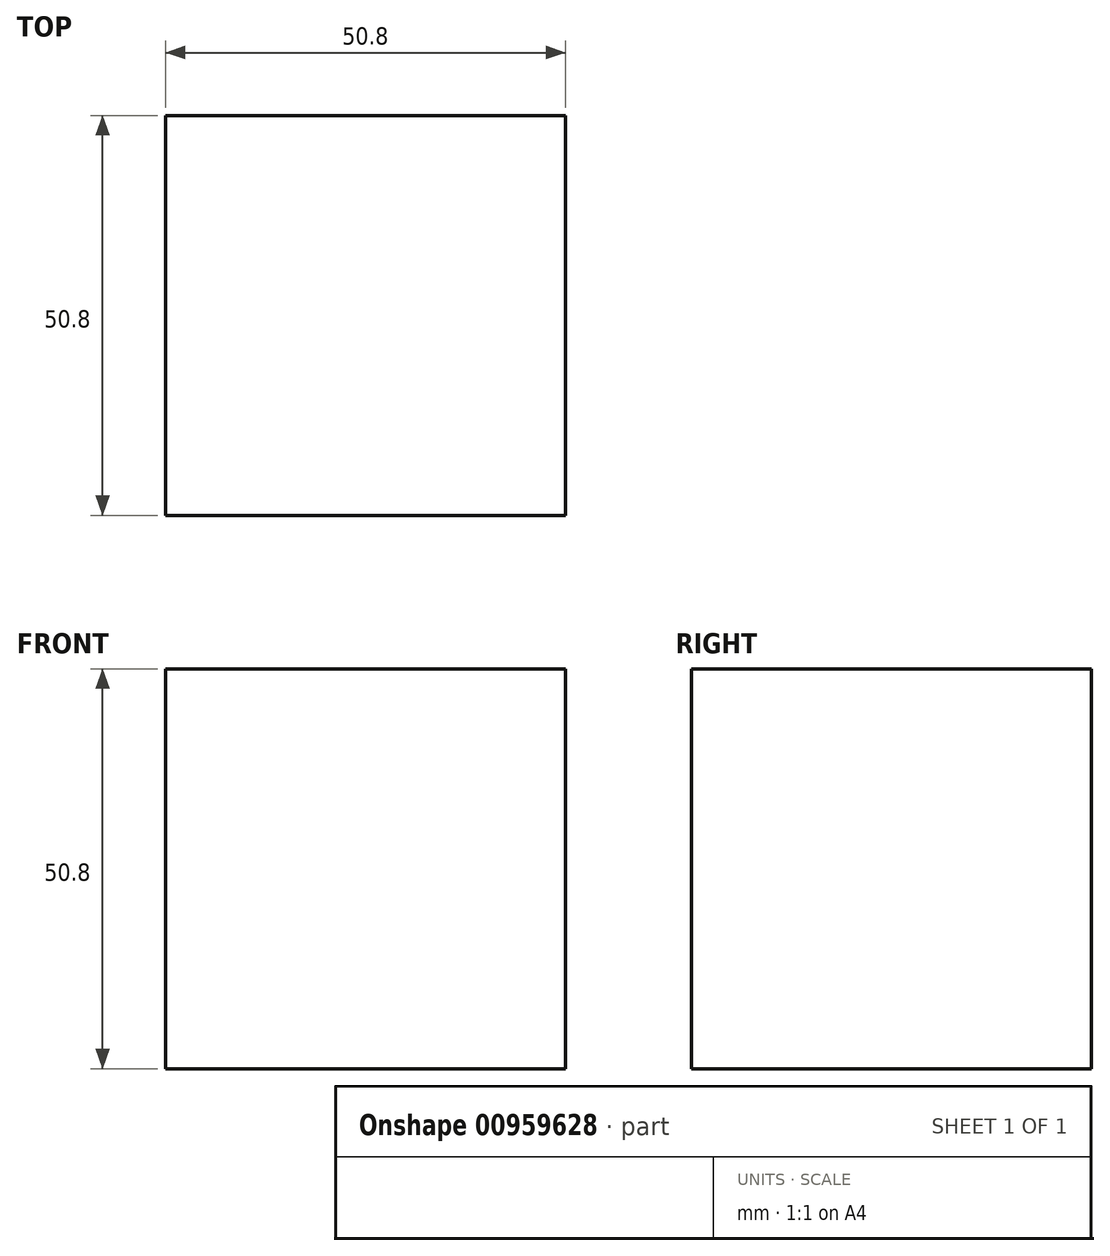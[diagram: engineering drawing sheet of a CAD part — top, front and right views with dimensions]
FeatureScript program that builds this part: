
annotation { "Feature Type Name" : "Feature", "Feature Type Description" : "" }
export const myFeature = defineFeature(function(context is Context, id is Id, definition is map)
    precondition{}
    {
        {
            var Q0;
            Q0=qCreatedBy(makeId("Top.planeOp"),FACE);
            var sketch = newSketch(context, id + "F0", { "sketchPlane" : qUnion([Q0])});
            skLineSegment(sketch, "E0.bottom", {"start": v(25.4, 25.4) * mm, "end": v(-25.4, 25.4) * mm});
            skLineSegment(sketch, "E0.top", {"start": v(25.4, -25.4) * mm, "end": v(-25.4, -25.4) * mm});
            skLineSegment(sketch, "E0.left", {"start": v(25.4, 25.4) * mm, "end": v(25.4, -25.4) * mm});
            skLineSegment(sketch, "E0.right", {"start": v(-25.4, 25.4) * mm, "end": v(-25.4, -25.4) * mm});
            skPoint(sketch, "E0.middle", {"position": v(0, 0) * mm});
            skSolve(sketch);
        }
        {
            var Q0;
            Q0=makeQuery(id+"F0.imprint","IMPRINT",FACE,{"disambiguationData":[TD([[makeQuery(id+"F0.imprint","IMPRINT",EDGE,{"derivedFrom":sQuery(id+"F0.wireOp",EDGE,"E0.bottom")}),1.0]])]});
            extrude(context, id + "F1", {"entities" : qUnion([Q0]), "depth" : 25.4 * mm, "offsetDistance" : 25.4 * mm, "hasSecondDirection" : true, "secondDirectionOppositeDirection" : true, "secondDirectionDepth" : 25.4 * mm});
        }
    });
